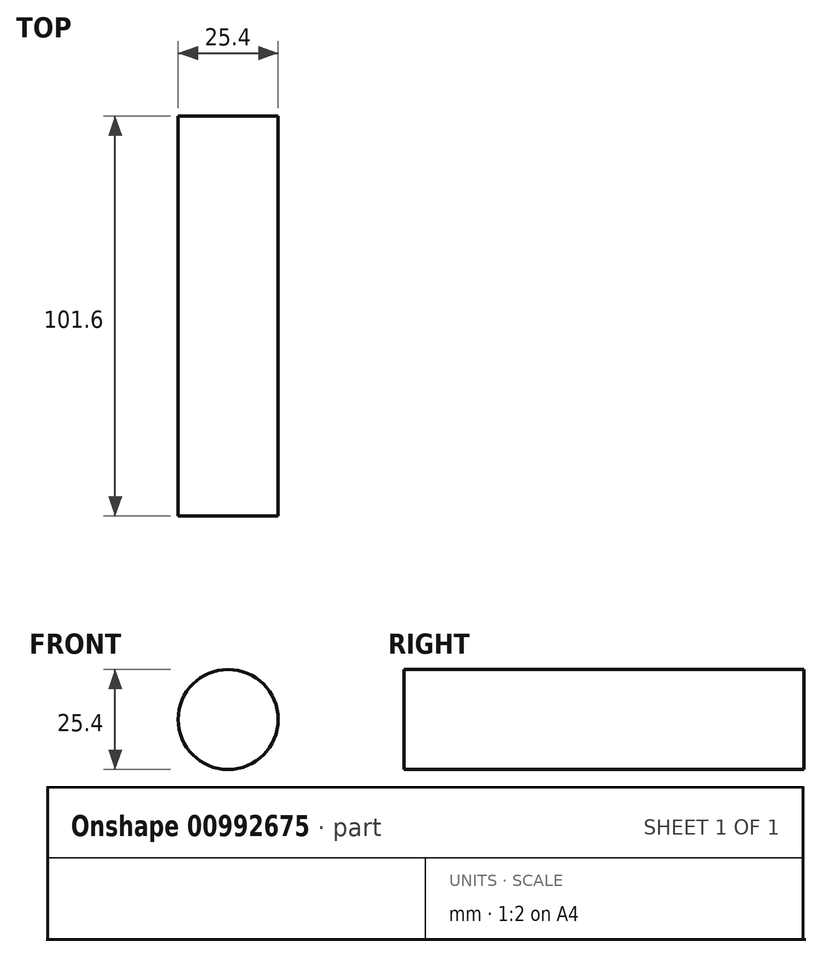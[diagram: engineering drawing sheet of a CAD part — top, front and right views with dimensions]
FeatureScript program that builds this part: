
annotation { "Feature Type Name" : "Feature", "Feature Type Description" : "" }
export const myFeature = defineFeature(function(context is Context, id is Id, definition is map)
    precondition{}
    {
        {
            var Q0;
            Q0=qCreatedBy(makeId("Front.planeOp"),FACE);
            var sketch = newSketch(context, id + "F0", { "sketchPlane" : qUnion([Q0])});
            skCircle(sketch, "E0", {"center": v(0, 0) * mm, "radius": 12.7 * mm});
            skSolve(sketch);
        }
        {
            var Q0;
            Q0=makeQuery(id+"F0.imprint","IMPRINT",FACE,{"disambiguationData":[TD([[makeQuery(id+"F0.imprint","IMPRINT",EDGE,{"derivedFrom":sQuery(id+"F0.wireOp",EDGE,"E0")}),1.0]])]});
            extrude(context, id + "F1", {"entities" : qUnion([Q0]), "depth" : 101.6 * mm, "offsetDistance" : 25.4 * mm});
        }
    });
